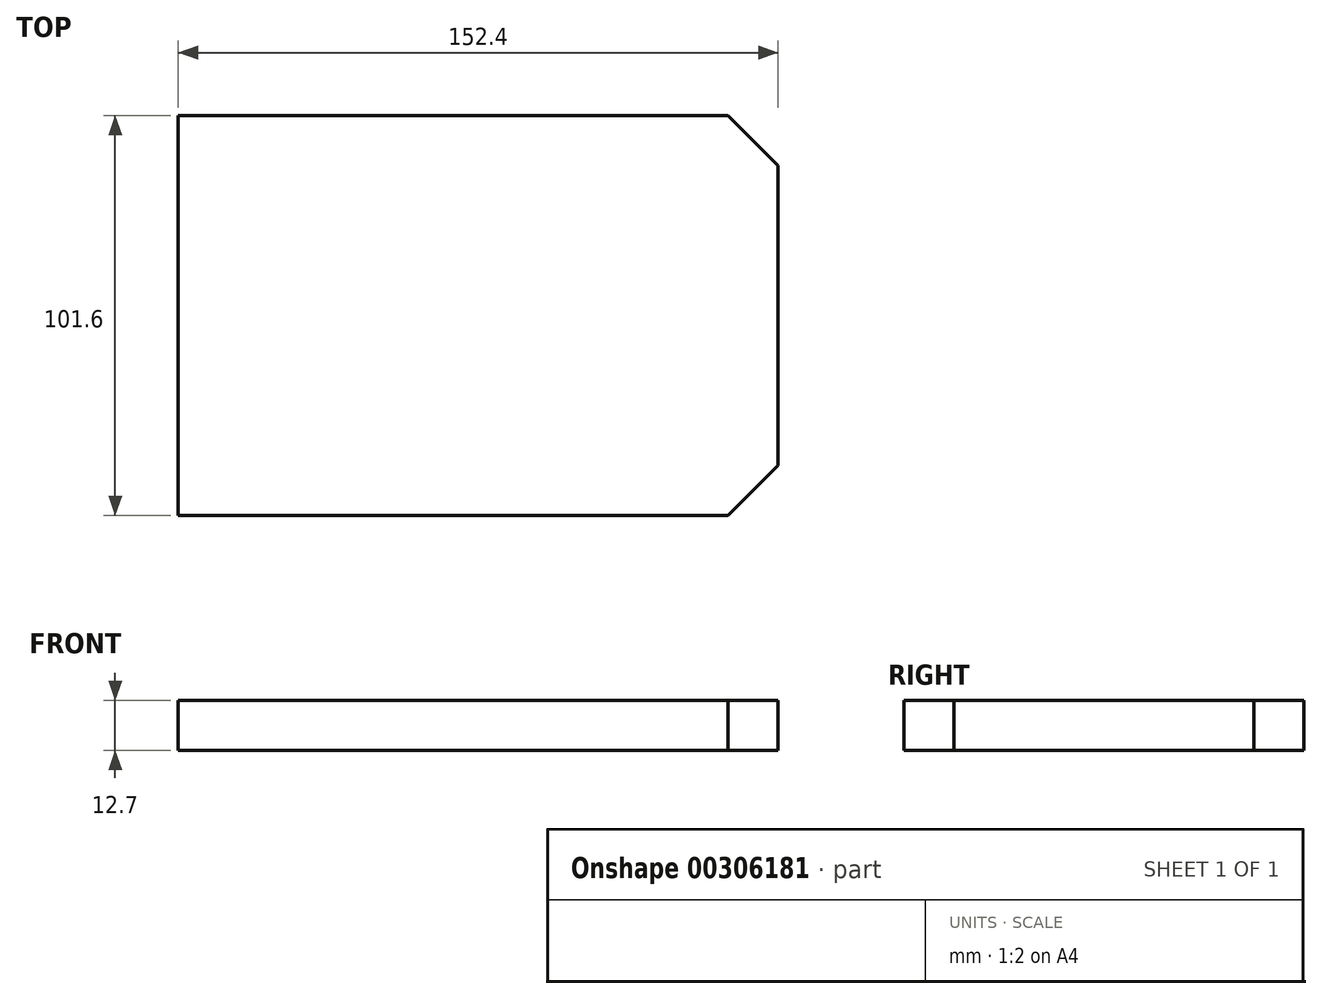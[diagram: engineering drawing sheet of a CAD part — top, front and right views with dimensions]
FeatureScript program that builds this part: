
annotation { "Feature Type Name" : "Feature", "Feature Type Description" : "" }
export const myFeature = defineFeature(function(context is Context, id is Id, definition is map)
    precondition{}
    {
        {
            var Q0;
            Q0=qCreatedBy(makeId("Front.planeOp"),FACE);
            var sketch = newSketch(context, id + "F0", { "sketchPlane" : qUnion([Q0])});
            skLineSegment(sketch, "E0.bottom", {"start": v(76.2, -6.35) * mm, "end": v(-76.2, -6.35) * mm});
            skLineSegment(sketch, "E0.top", {"start": v(76.2, 6.35) * mm, "end": v(-76.2, 6.35) * mm});
            skLineSegment(sketch, "E0.left", {"start": v(76.2, -6.35) * mm, "end": v(76.2, 6.35) * mm});
            skLineSegment(sketch, "E0.right", {"start": v(-76.2, -6.35) * mm, "end": v(-76.2, 6.35) * mm});
            skPoint(sketch, "E0.middle", {"position": v(0, 0) * mm});
            skSolve(sketch);
        }
        {
            var Q0;
            Q0=makeQuery(id+"F0.imprint","IMPRINT",FACE,{"disambiguationData":[TD([[makeQuery(id+"F0.imprint","IMPRINT",EDGE,{"derivedFrom":sQuery(id+"F0.wireOp",EDGE,"E0.bottom")}),-1.0]])]});
            extrude(context, id + "F1", {"entities" : qUnion([Q0]), "depth" : 101.6 * mm});
        }
        {
            var Q0;
            Q0=makeQuery(id+"F1.opExtrude","SWEPT_FACE",FACE,{"disambiguationData":[OSD([sQuery(id+"F0.wireOp",EDGE,"E0.top")])]});
            var sketch = newSketch(context, id + "F2", { "sketchPlane" : qUnion([Q0])});
            skLineSegment(sketch, "E1", {"start": v(76.2, -101.6) * mm, "end": v(63.5, -101.6) * mm});
            skLineSegment(sketch, "E2", {"start": v(63.5, -101.6) * mm, "end": v(76.2, -88.9) * mm});
            skLineSegment(sketch, "E3", {"start": v(76.2, -88.9) * mm, "end": v(76.2, -101.6) * mm});
            skLineSegment(sketch, "E4", {"start": v(76.2, 0) * mm, "end": v(76.2, -12.7) * mm});
            skLineSegment(sketch, "E5", {"start": v(76.2, -12.7) * mm, "end": v(63.5, 0) * mm});
            skLineSegment(sketch, "E6", {"start": v(63.5, 0) * mm, "end": v(76.2, 0) * mm});
            skSolve(sketch);
        }
        {
            var Q0;
            Q0=makeQuery(id+"F2.imprint","IMPRINT",FACE,{"disambiguationData":[TD([[makeQuery(id+"F2.imprint","IMPRINT",EDGE,{"derivedFrom":sQuery(id+"F2.wireOp",EDGE,"E1")}),-1.0]])]});
            var Q1;
            Q1=makeQuery(id+"F2.imprint","IMPRINT",FACE,{"disambiguationData":[TD([[makeQuery(id+"F2.imprint","IMPRINT",EDGE,{"derivedFrom":sQuery(id+"F2.wireOp",EDGE,"E4")}),1.0]])]});
            extrude(context, id + "F3", {"entities" : qUnion([Q0, Q1]), "operationType" : NewBodyOperationType.REMOVE, "endBound" : BoundingType.THROUGH_ALL, "oppositeDirection" : true, "depth" : 25.4 * mm});
        }
    });
